# Revit family: Furniture-Floor_Mount-Vanity-KOHLER-HELST-K-33527_1
name_source: partatom
category: Plumbing Fixtures
revit_build: Autodesk Revit 2017 (Build: 20160225_1515(x64)
units: mm (PartAtom-declared; Revit-internal decimal feet)

## family parameters
Cut with Voids When Loaded = No
Host = Face
OmniClass Number = 23.31.25.13
OmniClass Title = Bathroom Cabinets
Part Type = Normal
Room Calculation Point = No
Round Connector Dimension = Use Diameter
Shared = No

## types (2) — shared parameters
ADA Compliant = No
Assembly Code = D2010400
CW Connection = No
Cold Water Inlet = Cold Water Inlet
Date Modified = 02/16/2021
Default Elevation = 0"
Description = VANITY 60 INCHES
Drain Included = No
HW Connection = No
Hardware Included = Yes
Height = 35 13/16"
Hot Water Inlet = Hot Water Inlet
Length = 18 15/16"
Manufacturer = KOHLER Co.
Master Format 2014 = 22 41 16
Master Format 2014 Name = Residential Lavatories and Sinks
Material = Solid Wood
Product Documentation Link = https://www.us.kohler.com
Product Name = HELST
Product Page URL = http://www.us.kohler.com
URL = https://www.us.kohler.com
Vent Connection = No
Waste Connection = Yes
Waste Water Outlet 1 = Waste Water Outlet 1
Waste Water Outlet 2 = Waste Water Outlet 2
WaterSense Certified = No
Width = 60 1/8"

## per-type parameters (varying)
| type | Finish | Model | Type |
| 0- White | Kohler-Wood-Molded-0-White | K-33527-ASB-0 | 1 |
| 1WT- Mohair Grey | Kohler-Wood-1WT-Mohair_Grey | K-33527-ASB-1WT | 2 |

## geometry (parser evidence)
native form markers: Sweep x5
no freeform markers — native parametric forms only
